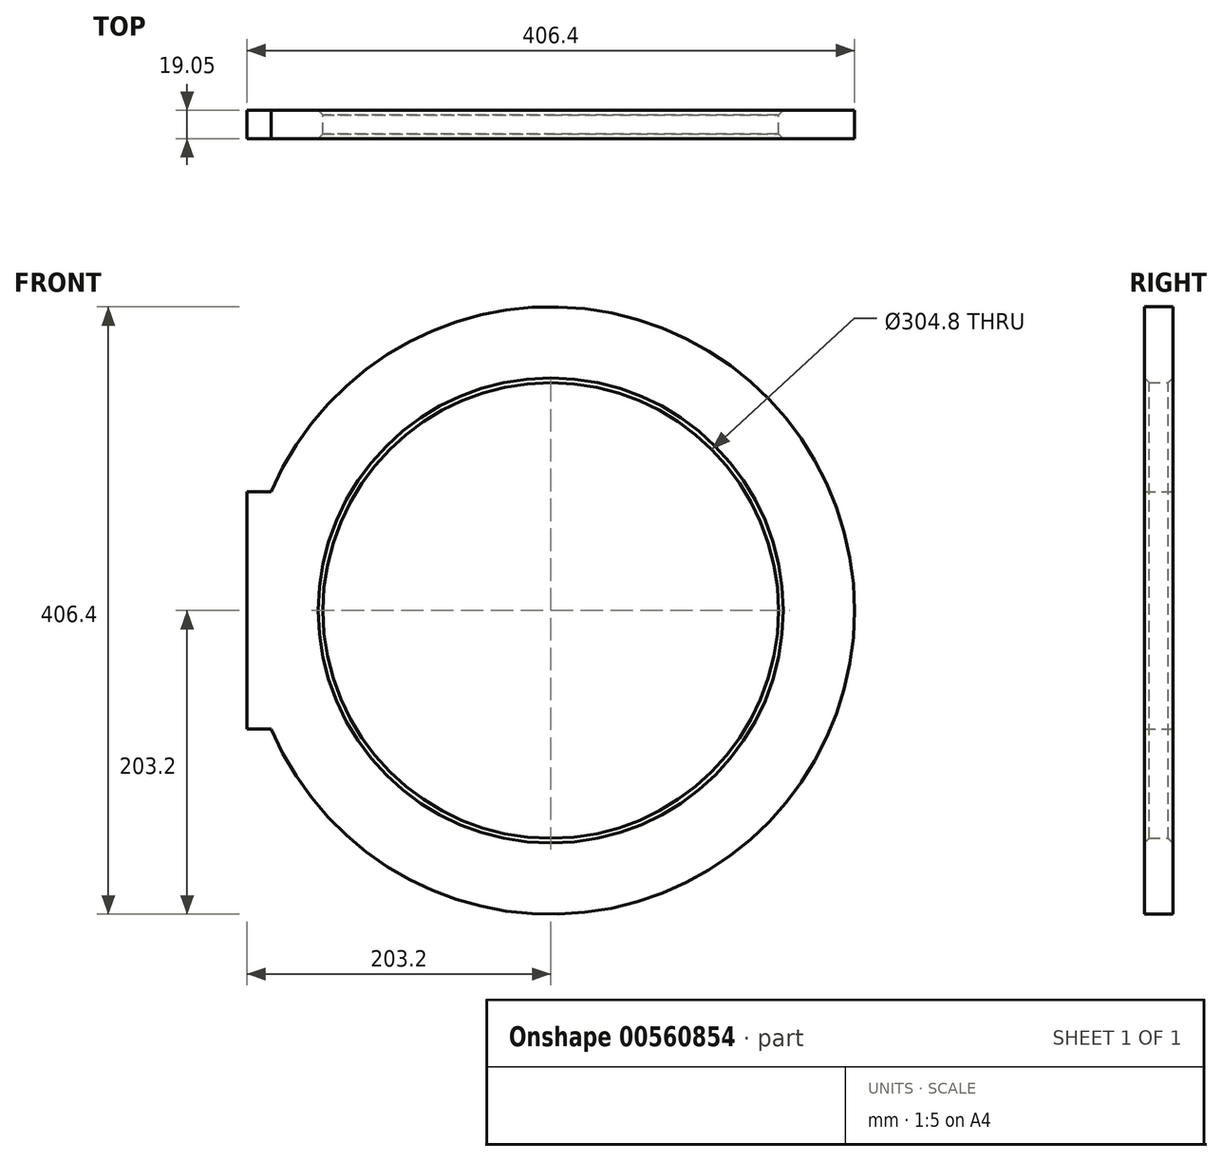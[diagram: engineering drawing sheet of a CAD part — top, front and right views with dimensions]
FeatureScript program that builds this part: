
annotation { "Feature Type Name" : "Feature", "Feature Type Description" : "" }
export const myFeature = defineFeature(function(context is Context, id is Id, definition is map)
    precondition{}
    {
        {
            var Q0;
            Q0=qCreatedBy(makeId("Front.planeOp"),FACE);
            var sketch = newSketch(context, id + "F0", { "sketchPlane" : qUnion([Q0])});
            skCircle(sketch, "E0", {"center": v(0, 0) * mm, "radius": 152.4 * mm});
            skArc(sketch, "E1", {"start": v(-187.06, -79.37) * mm, "mid": v(203.2, 0) * mm, "end": v(-187.06, 79.37) * mm});
            skLineSegment(sketch, "E2", {"start": v(-187.06, 79.38) * mm, "end": v(-203.2, 79.38) * mm});
            skLineSegment(sketch, "E3", {"start": v(-203.2, 79.38) * mm, "end": v(-203.2, -79.38) * mm});
            skLineSegment(sketch, "E4", {"start": v(-203.2, -79.38) * mm, "end": v(-187.06, -79.38) * mm});
            skLineSegment(sketch, "E5", {"start": v(-293.07, 0) * mm, "end": v(0, 0) * mm, "construction": true});
            skSolve(sketch);
        }
        {
            var Q0;
            Q0=qSketchRegion(id+"F0",true);
            extrude(context, id + "F1", {"entities" : qUnion([Q0]), "depth" : 19.05 * mm, "offsetDistance" : 25.4 * mm});
        }
        {
            var Q0;
            Q0=makeQuery(id+"F1.opExtrude","CAP_EDGE",EDGE,{"disambiguationData":[OSD([sQuery(id+"F0.wireOp",EDGE,"E0")])],"isStart":false});
            var Q1;
            Q1=makeQuery(id+"F1.opExtrude","CAP_EDGE",EDGE,{"disambiguationData":[OSD([sQuery(id+"F0.wireOp",EDGE,"E0")])],"isStart":true});
            chamfer(context, id + "F2", {"entities" : qUnion([Q0, Q1]), "width" : 3.17 * mm, "tangentPropagation" : true});
        }
    });
